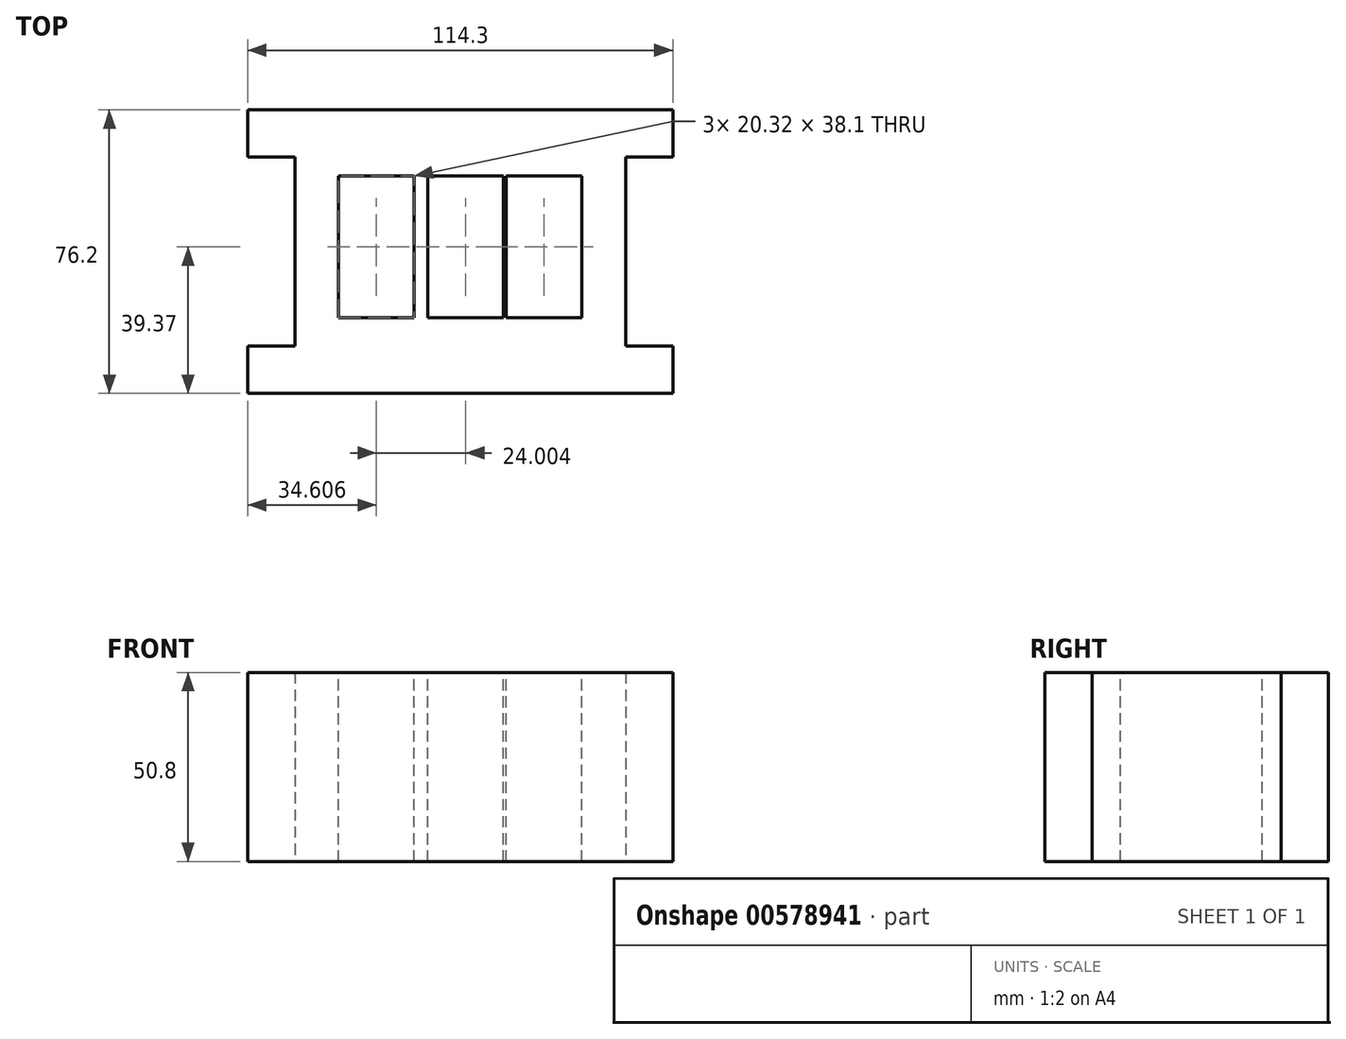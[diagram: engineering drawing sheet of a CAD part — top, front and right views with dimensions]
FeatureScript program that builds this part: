
annotation { "Feature Type Name" : "Feature", "Feature Type Description" : "" }
export const myFeature = defineFeature(function(context is Context, id is Id, definition is map)
    precondition{}
    {
        {
            var Q0;
            Q0=qCreatedBy(makeId("Top.planeOp"),FACE);
            var sketch = newSketch(context, id + "F0", { "sketchPlane" : qUnion([Q0])});
            skLineSegment(sketch, "E0", {"start": v(-114.3, 0) * mm, "end": v(0, 0) * mm});
            skLineSegment(sketch, "E1", {"start": v(0, 0) * mm, "end": v(0, -12.7) * mm});
            skLineSegment(sketch, "E2", {"start": v(0, -12.7) * mm, "end": v(-12.7, -12.7) * mm});
            skLineSegment(sketch, "E3", {"start": v(-12.7, -12.7) * mm, "end": v(-12.7, -63.5) * mm});
            skLineSegment(sketch, "E4", {"start": v(-12.7, -63.5) * mm, "end": v(0, -63.5) * mm});
            skLineSegment(sketch, "E5", {"start": v(0, -63.5) * mm, "end": v(0, -76.2) * mm});
            skLineSegment(sketch, "E6", {"start": v(0, -76.2) * mm, "end": v(-114.3, -76.2) * mm});
            skLineSegment(sketch, "E7", {"start": v(-114.3, -76.2) * mm, "end": v(-114.3, -63.5) * mm});
            skLineSegment(sketch, "E8", {"start": v(-114.3, -63.5) * mm, "end": v(-101.6, -63.5) * mm});
            skLineSegment(sketch, "E9", {"start": v(-101.6, -63.5) * mm, "end": v(-101.6, -12.7) * mm});
            skLineSegment(sketch, "E10", {"start": v(-101.6, -12.7) * mm, "end": v(-114.3, -12.7) * mm});
            skLineSegment(sketch, "E11", {"start": v(-114.3, -12.7) * mm, "end": v(-114.3, 0) * mm});
            skSolve(sketch);
        }
        {
            var Q0;
            Q0 = qSketchRegion(id + "F0", true);
            extrude(context, id + "F1", {"entities" : qUnion([Q0]), "depth" : 50.8 * mm, "offsetDistance" : 25.4 * mm});
        }
        {
            var Q0;
            Q0=makeQuery(id+"F1.opExtrude","CAP_FACE",FACE,{"disambiguationData":[OSD([sQuery(id+"F0.wireOp",EDGE,"E0"),sQuery(id+"F0.wireOp",EDGE,"E1"),sQuery(id+"F0.wireOp",EDGE,"E2"),sQuery(id+"F0.wireOp",EDGE,"E3"),sQuery(id+"F0.wireOp",EDGE,"E4"),sQuery(id+"F0.wireOp",EDGE,"E5"),sQuery(id+"F0.wireOp",EDGE,"E6"),sQuery(id+"F0.wireOp",EDGE,"E7"),sQuery(id+"F0.wireOp",EDGE,"E8"),sQuery(id+"F0.wireOp",EDGE,"E9"),sQuery(id+"F0.wireOp",EDGE,"E10"),sQuery(id+"F0.wireOp",EDGE,"E11")])],"isStart":false});
            var sketch = newSketch(context, id + "F2", { "sketchPlane" : qUnion([Q0])});
            skLineSegment(sketch, "E12.bottom", {"start": v(-89.85, -17.78) * mm, "end": v(-69.53, -17.78) * mm});
            skLineSegment(sketch, "E12.top", {"start": v(-89.85, -55.88) * mm, "end": v(-69.53, -55.88) * mm});
            skLineSegment(sketch, "E12.left", {"start": v(-89.85, -17.78) * mm, "end": v(-89.85, -55.88) * mm});
            skLineSegment(sketch, "E12.right", {"start": v(-69.53, -17.78) * mm, "end": v(-69.53, -55.88) * mm});
            skLineSegment(sketch, "E13.bottom", {"start": v(-65.85, -17.78) * mm, "end": v(-45.53, -17.78) * mm});
            skLineSegment(sketch, "E13.top", {"start": v(-65.85, -55.88) * mm, "end": v(-45.53, -55.88) * mm});
            skLineSegment(sketch, "E13.left", {"start": v(-65.85, -17.78) * mm, "end": v(-65.85, -55.88) * mm});
            skLineSegment(sketch, "E13.right", {"start": v(-45.53, -17.78) * mm, "end": v(-45.53, -55.88) * mm});
            skLineSegment(sketch, "E14.bottom", {"start": v(-44.77, -17.78) * mm, "end": v(-24.45, -17.78) * mm});
            skLineSegment(sketch, "E14.top", {"start": v(-44.77, -55.88) * mm, "end": v(-24.45, -55.88) * mm});
            skLineSegment(sketch, "E14.left", {"start": v(-44.77, -17.78) * mm, "end": v(-44.77, -55.88) * mm});
            skLineSegment(sketch, "E14.right", {"start": v(-24.45, -17.78) * mm, "end": v(-24.45, -55.88) * mm});
            skSolve(sketch);
        }
        {
            var Q0;
            Q0=makeQuery(id+"F2.imprint","IMPRINT",FACE,{"disambiguationData":[TD([[makeQuery(id+"F2.imprint","IMPRINT",EDGE,{"derivedFrom":sQuery(id+"F2.wireOp",EDGE,"E14.bottom")}),-1.0]])]});
            var Q1;
            Q1=makeQuery(id+"F2.imprint","IMPRINT",FACE,{"disambiguationData":[TD([[makeQuery(id+"F2.imprint","IMPRINT",EDGE,{"derivedFrom":sQuery(id+"F2.wireOp",EDGE,"E13.bottom")}),-1.0]])]});
            var Q2;
            Q2=makeQuery(id+"F2.imprint","IMPRINT",FACE,{"disambiguationData":[TD([[makeQuery(id+"F2.imprint","IMPRINT",EDGE,{"derivedFrom":sQuery(id+"F2.wireOp",EDGE,"E12.bottom")}),-1.0]])]});
            extrude(context, id + "F3", {"entities" : qUnion([Q0, Q1, Q2]), "operationType" : NewBodyOperationType.REMOVE, "oppositeDirection" : true, "depth" : 50.8 * mm, "offsetDistance" : 25.4 * mm});
        }
    });
